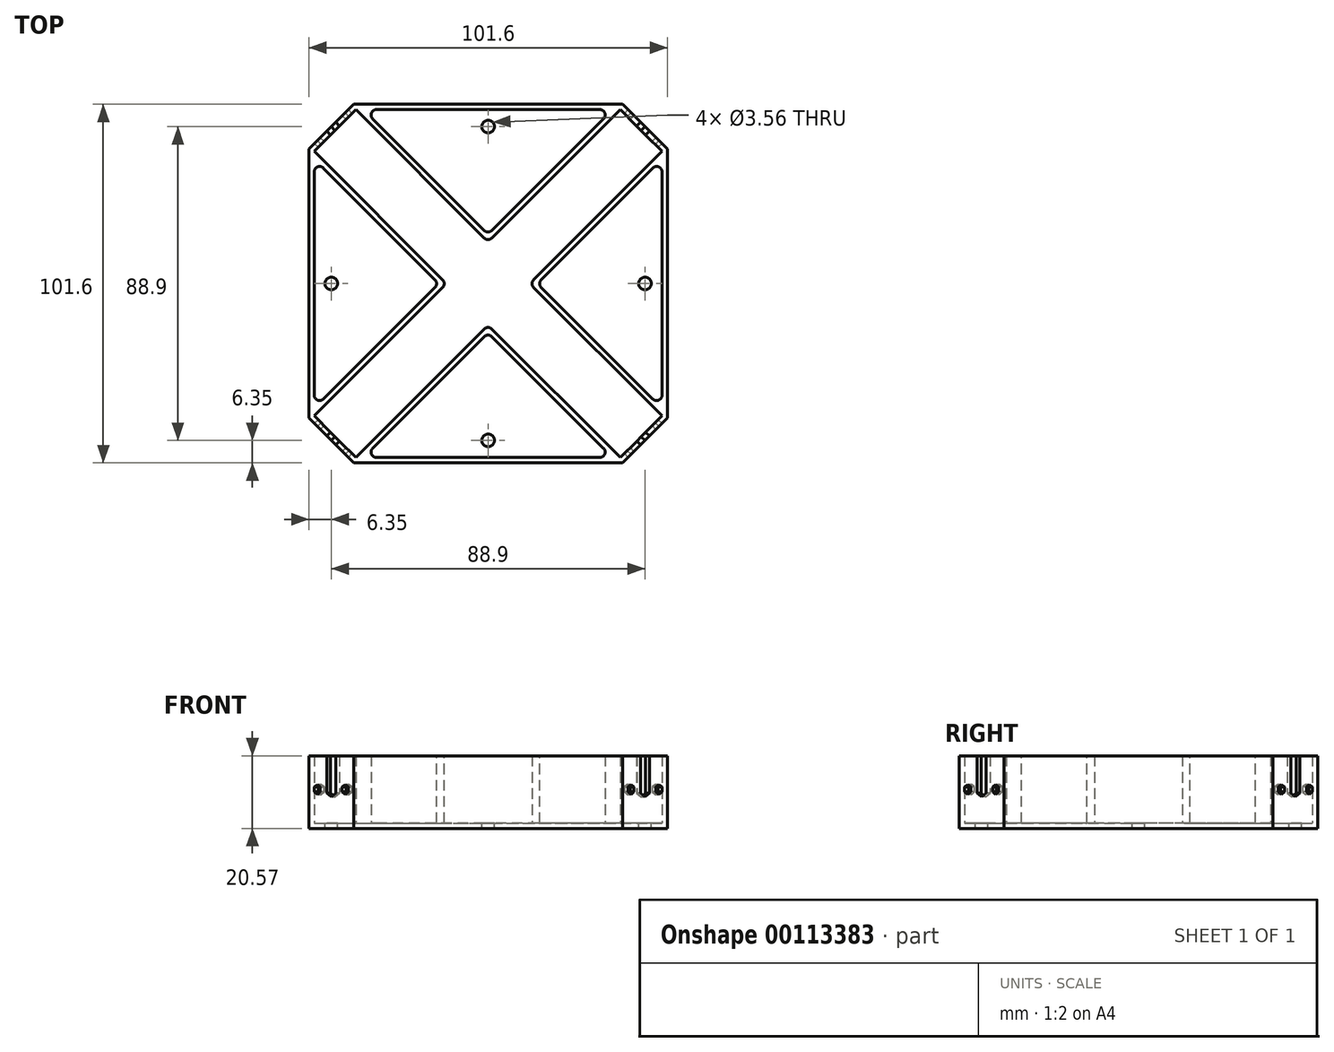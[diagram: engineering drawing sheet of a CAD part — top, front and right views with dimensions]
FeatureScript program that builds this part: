
annotation { "Feature Type Name" : "Feature", "Feature Type Description" : "" }
export const myFeature = defineFeature(function(context is Context, id is Id, definition is map)
    precondition{}
    {
        {
            var Q0;
            Q0=qCreatedBy(makeId("Top.planeOp"),FACE);
            var sketch = newSketch(context, id + "F0", { "sketchPlane" : qUnion([Q0])});
            skLineSegment(sketch, "E0.bottom", {"start": v(50.8, 50.8) * mm, "end": v(-50.8, 50.8) * mm});
            skLineSegment(sketch, "E0.top", {"start": v(50.8, -50.8) * mm, "end": v(-50.8, -50.8) * mm});
            skLineSegment(sketch, "E0.left", {"start": v(50.8, 50.8) * mm, "end": v(50.8, -50.8) * mm});
            skLineSegment(sketch, "E0.right", {"start": v(-50.8, 50.8) * mm, "end": v(-50.8, -50.8) * mm});
            skPoint(sketch, "E0.middle", {"position": v(0, 0) * mm});
            skLineSegment(sketch, "E1", {"start": v(-50.8, 38.1) * mm, "end": v(-38.1, 50.8) * mm});
            skLineSegment(sketch, "E2", {"start": v(38.1, 50.8) * mm, "end": v(50.8, 38.1) * mm});
            skLineSegment(sketch, "E3", {"start": v(38.1, -50.8) * mm, "end": v(50.8, -38.1) * mm});
            skLineSegment(sketch, "E4", {"start": v(-38.1, -50.8) * mm, "end": v(-50.8, -38.1) * mm});
            skLineSegment(sketch, "E5.0", {"start": v(-49.28, 37.47) * mm, "end": v(-37.47, 49.28) * mm});
            skLineSegment(sketch, "E6.0", {"start": v(37.47, 49.28) * mm, "end": v(49.28, 37.47) * mm});
            skLineSegment(sketch, "E7.0", {"start": v(-37.47, -49.28) * mm, "end": v(-49.28, -37.47) * mm});
            skLineSegment(sketch, "E8.0", {"start": v(37.47, -49.28) * mm, "end": v(49.28, -37.47) * mm});
            skLineSegment(sketch, "E9", {"start": v(-37.47, 49.28) * mm, "end": v(37.47, 49.28) * mm});
            skLineSegment(sketch, "E10", {"start": v(-49.28, 37.47) * mm, "end": v(-49.28, -37.47) * mm});
            skLineSegment(sketch, "E11", {"start": v(-37.47, -49.28) * mm, "end": v(37.47, -49.28) * mm});
            skLineSegment(sketch, "E12", {"start": v(49.28, -37.47) * mm, "end": v(49.28, 37.47) * mm});
            skLineSegment(sketch, "E13", {"start": v(-49.28, 37.47) * mm, "end": v(37.47, -49.28) * mm, "construction": true});
            skLineSegment(sketch, "E14", {"start": v(-37.47, 49.28) * mm, "end": v(49.28, -37.47) * mm, "construction": true});
            skLineSegment(sketch, "E15", {"start": v(37.47, 49.28) * mm, "end": v(-49.28, -37.47) * mm, "construction": true});
            skLineSegment(sketch, "E16", {"start": v(-37.47, -49.28) * mm, "end": v(49.28, 37.47) * mm, "construction": true});
            skLineSegment(sketch, "E17", {"start": v(-49.28, 37.47) * mm, "end": v(-11.8, 0) * mm});
            skLineSegment(sketch, "E18", {"start": v(-37.47, 49.28) * mm, "end": v(0, 11.8) * mm});
            skLineSegment(sketch, "E19", {"start": v(0, 11.8) * mm, "end": v(37.47, 49.28) * mm});
            skLineSegment(sketch, "E20", {"start": v(49.28, 37.47) * mm, "end": v(11.8, 0) * mm});
            skLineSegment(sketch, "E21", {"start": v(11.8, 0) * mm, "end": v(49.28, -37.47) * mm});
            skLineSegment(sketch, "E22", {"start": v(-49.28, -37.47) * mm, "end": v(-11.8, 0) * mm});
            skLineSegment(sketch, "E23", {"start": v(-37.47, -49.28) * mm, "end": v(0, -11.8) * mm});
            skLineSegment(sketch, "E24", {"start": v(0, -11.8) * mm, "end": v(37.47, -49.28) * mm});
            skLineSegment(sketch, "E25.0", {"start": v(-35.31, 49.28) * mm, "end": v(49.28, -35.31) * mm, "construction": true});
            skLineSegment(sketch, "E26.0", {"start": v(35.31, 49.28) * mm, "end": v(-49.28, -35.31) * mm, "construction": true});
            skLineSegment(sketch, "E27.0", {"start": v(-35.31, -49.28) * mm, "end": v(49.28, 35.31) * mm, "construction": true});
            skLineSegment(sketch, "E28.0", {"start": v(-49.28, 35.31) * mm, "end": v(35.31, -49.28) * mm, "construction": true});
            skLineSegment(sketch, "E29", {"start": v(-49.28, -35.31) * mm, "end": v(-13.96, 0) * mm});
            skLineSegment(sketch, "E30", {"start": v(-13.96, 0) * mm, "end": v(-49.28, 35.31) * mm});
            skLineSegment(sketch, "E31", {"start": v(-35.31, 49.28) * mm, "end": v(0, 13.96) * mm});
            skLineSegment(sketch, "E32", {"start": v(0, 13.96) * mm, "end": v(35.31, 49.28) * mm});
            skLineSegment(sketch, "E33", {"start": v(49.28, 35.31) * mm, "end": v(13.96, 0) * mm});
            skLineSegment(sketch, "E34", {"start": v(13.96, 0) * mm, "end": v(49.28, -35.31) * mm});
            skLineSegment(sketch, "E35", {"start": v(35.31, -49.28) * mm, "end": v(0, -13.96) * mm});
            skLineSegment(sketch, "E36", {"start": v(0, -13.96) * mm, "end": v(-35.31, -49.28) * mm});
            skSolve(sketch);
        }
        {
            var Q0;
            {var subQ15=sQuery(id+"F0.wireOp",EDGE,"E1");Q0=makeQuery(id+"F0.imprint","IMPRINT",FACE,{"disambiguationData":[TD([[makeQuery(id+"F0.imprint","IMPRINT",EDGE,{"derivedFrom":subQ15}),-1.0]])]});}
            var Q1;
            {var subQ0=sQuery(id+"F0.wireOp",EDGE,"E29");Q1=makeQuery(id+"F0.imprint","IMPRINT",FACE,{"disambiguationData":[TD([[makeQuery(id+"F0.imprint","IMPRINT",EDGE,{"derivedFrom":subQ0}),1.0]])]});}
            var Q2;
            {var subQ1=sQuery(id+"F0.wireOp",EDGE,"E17");Q2=makeQuery(id+"F0.imprint","IMPRINT",FACE,{"disambiguationData":[TD([[makeQuery(id+"F0.imprint","IMPRINT",EDGE,{"derivedFrom":subQ1}),-1.0]])]});}
            var Q3;
            Q3=makeQuery(id+"F0.imprint","IMPRINT",FACE,{"disambiguationData":[TD([[makeQuery(id+"F0.imprint","IMPRINT",EDGE,{"derivedFrom":sQuery(id+"F0.wireOp",EDGE,"E5.0")}),-1.0]])]});
            var Q4;
            {var subQ1=sQuery(id+"F0.wireOp",EDGE,"E18");Q4=makeQuery(id+"F0.imprint","IMPRINT",FACE,{"disambiguationData":[TD([[makeQuery(id+"F0.imprint","IMPRINT",EDGE,{"derivedFrom":subQ1}),1.0]])]});}
            var Q5;
            {var subQ0=sQuery(id+"F0.wireOp",EDGE,"E20");Q5=makeQuery(id+"F0.imprint","IMPRINT",FACE,{"disambiguationData":[TD([[makeQuery(id+"F0.imprint","IMPRINT",EDGE,{"derivedFrom":subQ0}),1.0]])]});}
            var Q6;
            {var subQ0=sQuery(id+"F0.wireOp",EDGE,"E31");Q6=makeQuery(id+"F0.imprint","IMPRINT",FACE,{"disambiguationData":[TD([[makeQuery(id+"F0.imprint","IMPRINT",EDGE,{"derivedFrom":subQ0}),1.0]])]});}
            var Q7;
            {var subQ3=sQuery(id+"F0.wireOp",EDGE,"E23");Q7=makeQuery(id+"F0.imprint","IMPRINT",FACE,{"disambiguationData":[TD([[makeQuery(id+"F0.imprint","IMPRINT",EDGE,{"derivedFrom":subQ3}),-1.0]])]});}
            var Q8;
            {var subQ0=sQuery(id+"F0.wireOp",EDGE,"E35");Q8=makeQuery(id+"F0.imprint","IMPRINT",FACE,{"disambiguationData":[TD([[makeQuery(id+"F0.imprint","IMPRINT",EDGE,{"derivedFrom":subQ0}),1.0]])]});}
            var Q9;
            {var subQ0=sQuery(id+"F0.wireOp",EDGE,"E33");Q9=makeQuery(id+"F0.imprint","IMPRINT",FACE,{"disambiguationData":[TD([[makeQuery(id+"F0.imprint","IMPRINT",EDGE,{"derivedFrom":subQ0}),1.0]])]});}
            extrude(context, id + "F1", {"entities" : qUnion([Q0, Q1, Q2, Q3, Q4, Q5, Q6, Q7, Q8, Q9]), "oppositeDirection" : true, "depth" : 1.52 * mm});
        }
        {
            var Q0;
            {var subQ15=sQuery(id+"F0.wireOp",EDGE,"E1");Q0=makeQuery(id+"F0.imprint","IMPRINT",FACE,{"disambiguationData":[TD([[makeQuery(id+"F0.imprint","IMPRINT",EDGE,{"derivedFrom":subQ15}),-1.0]])]});}
            var Q1;
            {var subQ1=sQuery(id+"F0.wireOp",EDGE,"E17");Q1=makeQuery(id+"F0.imprint","IMPRINT",FACE,{"disambiguationData":[TD([[makeQuery(id+"F0.imprint","IMPRINT",EDGE,{"derivedFrom":subQ1}),-1.0]])]});}
            var Q2;
            {var subQ1=sQuery(id+"F0.wireOp",EDGE,"E18");Q2=makeQuery(id+"F0.imprint","IMPRINT",FACE,{"disambiguationData":[TD([[makeQuery(id+"F0.imprint","IMPRINT",EDGE,{"derivedFrom":subQ1}),1.0]])]});}
            var Q3;
            {var subQ3=sQuery(id+"F0.wireOp",EDGE,"E23");Q3=makeQuery(id+"F0.imprint","IMPRINT",FACE,{"disambiguationData":[TD([[makeQuery(id+"F0.imprint","IMPRINT",EDGE,{"derivedFrom":subQ3}),-1.0]])]});}
            var Q4;
            {var subQ0=sQuery(id+"F0.wireOp",EDGE,"E20");Q4=makeQuery(id+"F0.imprint","IMPRINT",FACE,{"disambiguationData":[TD([[makeQuery(id+"F0.imprint","IMPRINT",EDGE,{"derivedFrom":subQ0}),1.0]])]});}
            extrude(context, id + "F2", {"entities" : qUnion([Q0, Q1, Q2, Q3, Q4]), "operationType" : NewBodyOperationType.ADD, "depth" : 19.05 * mm});
        }
        {
            var Q0;
            Q0=makeQuery(id+"F2.opExtrude","SWEPT_EDGE",EDGE,{"disambiguationData":[OSD([sQuery(id+"F0.wireOp",EDGE,"E9"),sQuery(id+"F0.wireOp",EDGE,"E31")])]});
            var Q1;
            Q1=makeQuery(id+"F2.opExtrude","SWEPT_EDGE",EDGE,{"disambiguationData":[OSD([sQuery(id+"F0.wireOp",EDGE,"E9"),sQuery(id+"F0.wireOp",EDGE,"E32")])]});
            var Q2;
            Q2=makeQuery(id+"F2.opExtrude","SWEPT_EDGE",EDGE,{"disambiguationData":[OSD([sQuery(id+"F0.wireOp",EDGE,"E31"),sQuery(id+"F0.wireOp",EDGE,"E32")])]});
            var Q3;
            Q3=makeQuery(id+"F2.opExtrude","SWEPT_EDGE",EDGE,{"disambiguationData":[OSD([sQuery(id+"F0.wireOp",EDGE,"E18"),sQuery(id+"F0.wireOp",EDGE,"E19")])]});
            fillet(context, id + "F3", {"entities" : qUnion([Q0, Q1, Q2, Q3]), "radius" : 1.52 * mm, "tangentPropagation" : true, "allowEdgeOverflow" : false});
        }
        {
            var Q0;
            Q0=makeQuery(id+"F2.opExtrude","SWEPT_EDGE",EDGE,{"disambiguationData":[OSD([sQuery(id+"F0.wireOp",EDGE,"E29"),sQuery(id+"F0.wireOp",EDGE,"E30")])]});
            var Q1;
            Q1=makeQuery(id+"F2.opExtrude","SWEPT_EDGE",EDGE,{"disambiguationData":[OSD([sQuery(id+"F0.wireOp",EDGE,"E17"),sQuery(id+"F0.wireOp",EDGE,"E22")])]});
            var Q2;
            Q2=makeQuery(id+"F2.opExtrude","SWEPT_EDGE",EDGE,{"disambiguationData":[OSD([sQuery(id+"F0.wireOp",EDGE,"E10"),sQuery(id+"F0.wireOp",EDGE,"E30")])]});
            var Q3;
            Q3=makeQuery(id+"F2.opExtrude","SWEPT_EDGE",EDGE,{"disambiguationData":[OSD([sQuery(id+"F0.wireOp",EDGE,"E10"),sQuery(id+"F0.wireOp",EDGE,"E29")])]});
            fillet(context, id + "F4", {"entities" : qUnion([Q0, Q1, Q2, Q3]), "radius" : 1.52 * mm, "tangentPropagation" : true, "allowEdgeOverflow" : false});
        }
        {
            var Q0;
            Q0=makeQuery(id+"F2.opExtrude","SWEPT_EDGE",EDGE,{"disambiguationData":[OSD([sQuery(id+"F0.wireOp",EDGE,"E11"),sQuery(id+"F0.wireOp",EDGE,"E35")])]});
            var Q1;
            Q1=makeQuery(id+"F2.opExtrude","SWEPT_EDGE",EDGE,{"disambiguationData":[OSD([sQuery(id+"F0.wireOp",EDGE,"E11"),sQuery(id+"F0.wireOp",EDGE,"E36")])]});
            var Q2;
            Q2=makeQuery(id+"F2.opExtrude","SWEPT_EDGE",EDGE,{"disambiguationData":[OSD([sQuery(id+"F0.wireOp",EDGE,"E35"),sQuery(id+"F0.wireOp",EDGE,"E36")])]});
            var Q3;
            Q3=makeQuery(id+"F2.opExtrude","SWEPT_EDGE",EDGE,{"disambiguationData":[OSD([sQuery(id+"F0.wireOp",EDGE,"E23"),sQuery(id+"F0.wireOp",EDGE,"E24")])]});
            fillet(context, id + "F5", {"entities" : qUnion([Q0, Q1, Q2, Q3]), "radius" : 1.52 * mm, "tangentPropagation" : true, "allowEdgeOverflow" : false});
        }
        {
            var Q0;
            Q0=makeQuery(id+"F2.opExtrude","SWEPT_EDGE",EDGE,{"disambiguationData":[OSD([sQuery(id+"F0.wireOp",EDGE,"E12"),sQuery(id+"F0.wireOp",EDGE,"E34")])]});
            var Q1;
            Q1=makeQuery(id+"F2.opExtrude","SWEPT_EDGE",EDGE,{"disambiguationData":[OSD([sQuery(id+"F0.wireOp",EDGE,"E12"),sQuery(id+"F0.wireOp",EDGE,"E33")])]});
            var Q2;
            Q2=makeQuery(id+"F2.opExtrude","SWEPT_EDGE",EDGE,{"disambiguationData":[OSD([sQuery(id+"F0.wireOp",EDGE,"E33"),sQuery(id+"F0.wireOp",EDGE,"E34")])]});
            var Q3;
            Q3=makeQuery(id+"F2.opExtrude","SWEPT_EDGE",EDGE,{"disambiguationData":[OSD([sQuery(id+"F0.wireOp",EDGE,"E20"),sQuery(id+"F0.wireOp",EDGE,"E21")])]});
            fillet(context, id + "F6", {"entities" : qUnion([Q0, Q1, Q2, Q3]), "radius" : 1.52 * mm, "tangentPropagation" : true, "allowEdgeOverflow" : false});
        }
        {
            var Q0;
            {var subQ0=sQuery(id+"F0.wireOp",EDGE,"E4");Q0=makeQuery(id+"F2.boolean.opBoolean","MERGE",FACE,{"derivedFrom":[makeQuery(id+"F1.opExtrude","SWEPT_FACE",FACE,{"disambiguationData":[OSD([subQ0])]}),makeQuery(id+"F2.opExtrude","SWEPT_FACE",FACE,{"disambiguationData":[OSD([subQ0])]})]});}
            cPlane(context, id + "F7", {"entities" : qUnion([Q0]), "cplaneType" : CPlaneType.OFFSET, "offset" : 0 * mm, "width" : 152.4 * mm, "height" : 152.4 * mm});
        }
        {
            var Q0;
            Q0=qCreatedBy(id+"F7.planeOp",FACE);
            var sketch = newSketch(context, id + "F8", { "sketchPlane" : qUnion([Q0])});
            skLineSegment(sketch, "E37", {"start": v(-8.98, 9.53) * mm, "end": v(8.98, 9.53) * mm, "construction": true});
            skPoint(sketch, "E38", {"position": v(0, 9.53) * mm});
            skCircle(sketch, "E39.cCircle", {"center": v(0, 9.53) * mm, "radius": 1.78 * mm, "construction": true});
            skLineSegment(sketch, "E39.0", {"start": v(1.78, 10.55) * mm, "end": v(1.78, 8.5) * mm});
            skLineSegment(sketch, "E39.1", {"start": v(1.78, 8.5) * mm, "end": v(0, 7.47) * mm});
            skLineSegment(sketch, "E39.2", {"start": v(0, 7.47) * mm, "end": v(-1.78, 8.5) * mm});
            skLineSegment(sketch, "E39.3", {"start": v(-1.78, 8.5) * mm, "end": v(-1.78, 10.55) * mm});
            skLineSegment(sketch, "E39.4", {"start": v(-1.78, 10.55) * mm, "end": v(0, 11.58) * mm});
            skLineSegment(sketch, "E39.5", {"start": v(0, 11.58) * mm, "end": v(1.78, 10.55) * mm});
            skPoint(sketch, "E39.0.midPoint", {"position": v(1.78, 9.53) * mm});
            skCircle(sketch, "E40.cCircle", {"center": v(-5.59, 9.53) * mm, "radius": 1.2 * mm, "construction": true});
            skLineSegment(sketch, "E40.0", {"start": v(-4.4, 10.21) * mm, "end": v(-4.4, 8.84) * mm});
            skLineSegment(sketch, "E40.1", {"start": v(-4.4, 8.84) * mm, "end": v(-5.59, 8.15) * mm});
            skLineSegment(sketch, "E40.2", {"start": v(-5.59, 8.15) * mm, "end": v(-6.78, 8.84) * mm});
            skLineSegment(sketch, "E40.3", {"start": v(-6.78, 8.84) * mm, "end": v(-6.78, 10.21) * mm});
            skLineSegment(sketch, "E40.4", {"start": v(-6.78, 10.21) * mm, "end": v(-5.59, 10.9) * mm});
            skLineSegment(sketch, "E40.5", {"start": v(-5.59, 10.9) * mm, "end": v(-4.4, 10.21) * mm});
            skPoint(sketch, "E40.0.midPoint", {"position": v(-4.4, 9.53) * mm});
            skCircle(sketch, "E41.cCircle", {"center": v(5.59, 9.53) * mm, "radius": 1.2 * mm, "construction": true});
            skLineSegment(sketch, "E41.0", {"start": v(6.78, 10.21) * mm, "end": v(6.78, 8.84) * mm});
            skLineSegment(sketch, "E41.1", {"start": v(6.78, 8.84) * mm, "end": v(5.59, 8.15) * mm});
            skLineSegment(sketch, "E41.2", {"start": v(5.59, 8.15) * mm, "end": v(4.4, 8.84) * mm});
            skLineSegment(sketch, "E41.3", {"start": v(4.4, 8.84) * mm, "end": v(4.4, 10.21) * mm});
            skLineSegment(sketch, "E41.4", {"start": v(4.4, 10.21) * mm, "end": v(5.59, 10.9) * mm});
            skLineSegment(sketch, "E41.5", {"start": v(5.59, 10.9) * mm, "end": v(6.78, 10.21) * mm});
            skPoint(sketch, "E41.0.midPoint", {"position": v(6.78, 9.53) * mm});
            skLineSegment(sketch, "E42", {"start": v(-1.78, 10.55) * mm, "end": v(-1.78, 19.05) * mm});
            skLineSegment(sketch, "E43", {"start": v(1.78, 10.55) * mm, "end": v(1.78, 19.05) * mm});
            skLineSegment(sketch, "E44", {"start": v(-1.78, 19.05) * mm, "end": v(1.78, 19.05) * mm});
            skSolve(sketch);
        }
        {
            var Q0;
            Q0=makeQuery(id+"F8.imprint","IMPRINT",FACE,{"disambiguationData":[TD([[makeQuery(id+"F8.imprint","IMPRINT",EDGE,{"derivedFrom":sQuery(id+"F8.wireOp",EDGE,"E40.0")}),-1.0]])]});
            var Q1;
            Q1=makeQuery(id+"F8.imprint","IMPRINT",FACE,{"disambiguationData":[TD([[makeQuery(id+"F8.imprint","IMPRINT",EDGE,{"derivedFrom":sQuery(id+"F8.wireOp",EDGE,"E39.0")}),-1.0]])]});
            var Q2;
            Q2=makeQuery(id+"F8.imprint","IMPRINT",FACE,{"disambiguationData":[TD([[makeQuery(id+"F8.imprint","IMPRINT",EDGE,{"derivedFrom":sQuery(id+"F8.wireOp",EDGE,"E39.4")}),1.0]])]});
            var Q3;
            Q3=makeQuery(id+"F8.imprint","IMPRINT",FACE,{"disambiguationData":[TD([[makeQuery(id+"F8.imprint","IMPRINT",EDGE,{"derivedFrom":sQuery(id+"F8.wireOp",EDGE,"E41.0")}),-1.0]])]});
            extrude(context, id + "F9", {"entities" : qUnion([Q0, Q1, Q2, Q3]), "operationType" : NewBodyOperationType.REMOVE, "oppositeDirection" : true, "depth" : 127 * mm});
        }
        {
            var Q0;
            {var subQ0=sQuery(id+"F0.wireOp",EDGE,"E3");Q0=makeQuery(id+"F2.boolean.opBoolean","MERGE",FACE,{"derivedFrom":[makeQuery(id+"F1.opExtrude","SWEPT_FACE",FACE,{"disambiguationData":[OSD([subQ0])]}),makeQuery(id+"F2.opExtrude","SWEPT_FACE",FACE,{"disambiguationData":[OSD([subQ0])]})]});}
            cPlane(context, id + "F10", {"entities" : qUnion([Q0]), "cplaneType" : CPlaneType.OFFSET, "offset" : 0 * mm, "width" : 152.4 * mm, "height" : 152.4 * mm});
        }
        {
            var Q0;
            Q0=qCreatedBy(id+"F10.planeOp",FACE);
            var sketch = newSketch(context, id + "F11", { "sketchPlane" : qUnion([Q0])});
            skLineSegment(sketch, "E45", {"start": v(-8.98, 9.53) * mm, "end": v(8.98, 9.53) * mm, "construction": true});
            skPoint(sketch, "E46", {"position": v(0, 9.53) * mm});
            skCircle(sketch, "E47.cCircle", {"center": v(0, 9.53) * mm, "radius": 1.78 * mm, "construction": true});
            skLineSegment(sketch, "E47.0", {"start": v(1.78, 10.55) * mm, "end": v(1.78, 8.5) * mm});
            skLineSegment(sketch, "E47.1", {"start": v(1.78, 8.5) * mm, "end": v(0, 7.47) * mm});
            skLineSegment(sketch, "E47.2", {"start": v(0, 7.47) * mm, "end": v(-1.78, 8.5) * mm});
            skLineSegment(sketch, "E47.3", {"start": v(-1.78, 8.5) * mm, "end": v(-1.78, 10.55) * mm});
            skLineSegment(sketch, "E47.4", {"start": v(-1.78, 10.55) * mm, "end": v(0, 11.58) * mm});
            skLineSegment(sketch, "E47.5", {"start": v(0, 11.58) * mm, "end": v(1.78, 10.55) * mm});
            skPoint(sketch, "E47.0.midPoint", {"position": v(1.78, 9.53) * mm});
            skCircle(sketch, "E48.cCircle", {"center": v(5.59, 9.53) * mm, "radius": 1.2 * mm, "construction": true});
            skLineSegment(sketch, "E48.0", {"start": v(6.78, 10.21) * mm, "end": v(6.78, 8.84) * mm});
            skLineSegment(sketch, "E48.1", {"start": v(6.78, 8.84) * mm, "end": v(5.59, 8.15) * mm});
            skLineSegment(sketch, "E48.2", {"start": v(5.59, 8.15) * mm, "end": v(4.4, 8.84) * mm});
            skLineSegment(sketch, "E48.3", {"start": v(4.4, 8.84) * mm, "end": v(4.4, 10.21) * mm});
            skLineSegment(sketch, "E48.4", {"start": v(4.4, 10.21) * mm, "end": v(5.59, 10.9) * mm});
            skLineSegment(sketch, "E48.5", {"start": v(5.59, 10.9) * mm, "end": v(6.78, 10.21) * mm});
            skPoint(sketch, "E48.0.midPoint", {"position": v(6.78, 9.53) * mm});
            skCircle(sketch, "E49.cCircle", {"center": v(-5.59, 9.53) * mm, "radius": 1.2 * mm, "construction": true});
            skLineSegment(sketch, "E49.0", {"start": v(-4.4, 10.21) * mm, "end": v(-4.4, 8.84) * mm});
            skLineSegment(sketch, "E49.1", {"start": v(-4.4, 8.84) * mm, "end": v(-5.59, 8.15) * mm});
            skLineSegment(sketch, "E49.2", {"start": v(-5.59, 8.15) * mm, "end": v(-6.78, 8.84) * mm});
            skLineSegment(sketch, "E49.3", {"start": v(-6.78, 8.84) * mm, "end": v(-6.78, 10.21) * mm});
            skLineSegment(sketch, "E49.4", {"start": v(-6.78, 10.21) * mm, "end": v(-5.59, 10.9) * mm});
            skLineSegment(sketch, "E49.5", {"start": v(-5.59, 10.9) * mm, "end": v(-4.4, 10.21) * mm});
            skPoint(sketch, "E49.0.midPoint", {"position": v(-4.4, 9.53) * mm});
            skLineSegment(sketch, "E50", {"start": v(-1.78, 10.55) * mm, "end": v(-1.78, 19.05) * mm});
            skLineSegment(sketch, "E51", {"start": v(1.78, 10.55) * mm, "end": v(1.78, 19.05) * mm});
            skLineSegment(sketch, "E52", {"start": v(-1.78, 19.05) * mm, "end": v(1.78, 19.05) * mm});
            skSolve(sketch);
        }
        {
            var Q0;
            Q0=makeQuery(id+"F11.imprint","IMPRINT",FACE,{"disambiguationData":[TD([[makeQuery(id+"F11.imprint","IMPRINT",EDGE,{"derivedFrom":sQuery(id+"F11.wireOp",EDGE,"E49.0")}),-1.0]])]});
            var Q1;
            Q1=makeQuery(id+"F11.imprint","IMPRINT",FACE,{"disambiguationData":[TD([[makeQuery(id+"F11.imprint","IMPRINT",EDGE,{"derivedFrom":sQuery(id+"F11.wireOp",EDGE,"E47.4")}),1.0]])]});
            var Q2;
            Q2=makeQuery(id+"F11.imprint","IMPRINT",FACE,{"disambiguationData":[TD([[makeQuery(id+"F11.imprint","IMPRINT",EDGE,{"derivedFrom":sQuery(id+"F11.wireOp",EDGE,"E47.0")}),-1.0]])]});
            var Q3;
            Q3=makeQuery(id+"F11.imprint","IMPRINT",FACE,{"disambiguationData":[TD([[makeQuery(id+"F11.imprint","IMPRINT",EDGE,{"derivedFrom":sQuery(id+"F11.wireOp",EDGE,"E48.0")}),-1.0]])]});
            extrude(context, id + "F12", {"entities" : qUnion([Q0, Q1, Q2, Q3]), "operationType" : NewBodyOperationType.REMOVE, "oppositeDirection" : true, "depth" : 127 * mm});
        }
        {
            var Q0;
            Q0=qCreatedBy(makeId("Top.planeOp"),FACE);
            var sketch = newSketch(context, id + "F13", { "sketchPlane" : qUnion([Q0])});
            skCircle(sketch, "E53", {"center": v(0, 44.45) * mm, "radius": 1.78 * mm});
            skCircle(sketch, "E54", {"center": v(44.45, 0) * mm, "radius": 1.78 * mm});
            skCircle(sketch, "E55", {"center": v(0, -44.45) * mm, "radius": 1.78 * mm});
            skCircle(sketch, "E56", {"center": v(-44.45, 0) * mm, "radius": 1.78 * mm});
            skSolve(sketch);
        }
        {
            var Q0;
            Q0=makeQuery(id+"F13.imprint","IMPRINT",FACE,{"disambiguationData":[TD([[makeQuery(id+"F13.imprint","IMPRINT",EDGE,{"derivedFrom":sQuery(id+"F13.wireOp",EDGE,"E56")}),1.0]])]});
            var Q1;
            Q1=makeQuery(id+"F13.imprint","IMPRINT",FACE,{"disambiguationData":[TD([[makeQuery(id+"F13.imprint","IMPRINT",EDGE,{"derivedFrom":sQuery(id+"F13.wireOp",EDGE,"E53")}),1.0]])]});
            var Q2;
            Q2=makeQuery(id+"F13.imprint","IMPRINT",FACE,{"disambiguationData":[TD([[makeQuery(id+"F13.imprint","IMPRINT",EDGE,{"derivedFrom":sQuery(id+"F13.wireOp",EDGE,"E54")}),1.0]])]});
            var Q3;
            Q3=makeQuery(id+"F13.imprint","IMPRINT",FACE,{"disambiguationData":[TD([[makeQuery(id+"F13.imprint","IMPRINT",EDGE,{"derivedFrom":sQuery(id+"F13.wireOp",EDGE,"E55")}),1.0]])]});
            extrude(context, id + "F14", {"entities" : qUnion([Q0, Q1, Q2, Q3]), "operationType" : NewBodyOperationType.REMOVE, "oppositeDirection" : true, "depth" : 1.52 * mm});
        }
    });
